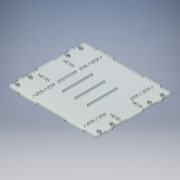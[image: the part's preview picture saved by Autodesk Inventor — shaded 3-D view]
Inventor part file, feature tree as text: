
AUTODESK INVENTOR PART (.ipt)
format: ipt  version: 2019 (Build 230136000, 136)  size: 1,142,784 bytes
history: native  units: mm
features: extrude x15, sketch x14, projected_geometry x12
ambient origin geometry x8: Origin, YZ Plane, XZ Plane, XY Plane, X Axis, Y Axis, Z Axis, Center Point
bodies: Body1 (feature_tree)
feature tree (41):
  extrude  "Extrusion2"  Depth=260.0mm
  extrude  "Extrusion3"  Depth=50.0mm
  extrude  "Extrusion5"  Depth=180.0mm
  extrude  "Extrusion7"  Depth=5.0mm
  extrude  "Extrusion8"  Depth=25.0mm
  extrude  "Extrusion9"  Depth=60.0mm
  extrude  "Extrusion10"  Depth=5.0mm
  extrude  "Extrusion11"  Depth=5.0mm
  extrude  "Extrusion12"  Depth=25.0mm
  extrude  "Extrusion13"  Depth=5.0mm TaperAngle=0.0deg
  extrude  "Extrusion14"  Depth=5.0mm
  extrude  "Extrusion15"  Depth=10.0mm TaperAngle=0.0deg
  extrude  "Extrusion16"  Depth=20.0mm
  extrude  "Extrusion17"  Depth=20.0mm
  extrude  "Extrusion19"  Depth=5.0mm TaperAngle=0.0deg
  sketch  "Sketch1"  dims[d7=280.0mm d8=260.0mm]
  sketch  "Sketch2"  dims[d11=170.0mm d12=50.0mm]
  projected_geometry  "Projected Loop1"
  sketch  "Sketch3"  dims[d22=5.0mm d23=0.0mm d24=180.0mm]
  projected_geometry  "Projected Loop2"
  sketch  "Sketch6"  dims[d25=50.0mm d26=5.0mm]
  projected_geometry  "Projected Loop4"
  sketch  "Sketch7"  dims[d27=60.0mm d28=25.0mm]
  projected_geometry  "Projected Loop5"
  sketch  "Sketch8"  dims[d29=5.0mm d30=60.0mm]
  projected_geometry  "Projected Loop6"
  projected_geometry  "Projected Loop7"
  sketch  "Sketch10"  dims[d31=25.0mm d32=5.0mm]
  sketch  "Sketch11"  dims[d33=60.0mm d34=5.0mm]
  projected_geometry  "Projected Loop8"
  sketch  "Sketch12"  dims[d35=60.0mm d36=25.0mm]
  sketch  "Sketch13"  dims[d37=25.0mm d38=5.0mm d39=0.0mm]
  projected_geometry  "Projected Loop9"
  sketch  "Sketch14"  dims[d40=20.0mm d41=5.0mm]
  projected_geometry  "Projected Loop10"
  sketch  "Sketch15"  dims[d43=15.0mm d46=10.0mm d47=0.0mm]
  projected_geometry  "Projected Loop11"
  sketch  "Sketch16"  dims[d48=30.0mm d51=20.0mm]
  projected_geometry  "Projected Loop12"
  sketch  "Sketch18"  dims[d52=10.0mm d53=0.0mm d54=20.0mm d55=5.0mm d56=0.0mm d57=260.0mm d58=80.0mm d59=20.0mm d60=0.0mm d61=20.0mm d65=20.0mm d66=4.0mm d67=4.0mm d68=10.0mm d69=20.0mm d70=4.0mm d71=4.0mm d72=20.0mm d73=4.0mm d74=4.0mm d75=20.0mm d76=4.0mm d77=4.0mm d78=5.0mm d79=0.0mm d80=20.0mm d81=20.0mm d82=4.0mm d83=4.0mm d84=10.0mm d85=20.0mm d86=4.0mm d87=4.0mm d88=20.0mm d89=4.0mm d90=4.0mm d91=20.0mm d92=4.0mm d93=4.0mm d94=5.0mm d95=0.0mm d96=4.0mm d97=6.0mm d98=4.0mm d99=6.0mm d100=10.0mm d101=0.0mm d102=18.0mm d103=5.0mm d104=90.0mm d105=16.0mm d106=16.0mm d107=4.0mm d108=4.0mm d109=6.0mm d110=6.0mm d111=10.0mm d112=0.0mm d113=17.0mm d114=4.0mm d115=4.0mm d116=8.0mm d118=17.0mm d119=4.0mm d120=4.0mm d121=8.0mm d122=17.0mm d123=4.0mm d124=4.0mm d125=8.0mm d126=17.0mm d127=4.0mm d128=4.0mm d129=8.0mm d133=20.0mm d134=40.0mm d135=20.0mm d136=40.0mm d137=10.0mm d138=0.0mm d139=3.5mm d140=20.0mm d141=3.5mm d142=20.0mm d143=3.5mm d144=60.0mm d145=30.0mm d146=5.0mm d147=0.0mm d148=60.0mm d149=3.5mm d150=60.0mm d151=3.5mm d152=40.0mm d153=40.0mm d154=5.0mm d155=0.0mm d156=5.0mm d157=60.0mm d158=15.0mm d159=5.0mm d160=0.0mm d161=0.0mm d162=4.0mm d163=0.0mm d164=0.0mm d165=4.0mm d166=0.0mm d167=0.0mm d168=4.0mm d169=0.0mm d170=4.0mm d171=10.0mm d172=10.0mm d185=3.5mm d186=100.0mm d187=40.0mm d188=3.5mm d189=100.0mm d190=3.5mm d191=100.0mm d192=40.0mm d193=5.0mm d194=0.0mm]
  projected_geometry  "Projected Loop14"
